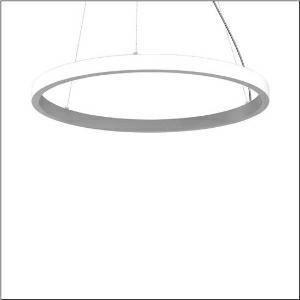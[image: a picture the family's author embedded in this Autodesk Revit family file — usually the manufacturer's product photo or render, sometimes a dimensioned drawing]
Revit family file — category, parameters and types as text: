
# Revit family: silica_r__21_ring-o_5pjbo4d1204a_97b4
name_source: partatom
category: Lighting Fixtures
units: mm (PartAtom-declared; Revit-internal decimal feet)

## family parameters
Cut with Voids When Loaded = No
Host = Face
Light Source = No
Part Type = Normal
Room Calculation Point = No
Round Connector Dimension = Use Diameter
Shared = No

## types (1)
- Silica® 21 Ring-O (1 x LED, 8820 lm, 343 W, 3000K)
    Apparent Load = 343 VA
    CIE Flux Codes = 2 16 49 50 100
    Color Rendering = 80
    Color Temperature = 3000K
    Default Elevation = 1800 mm
    Description = Silica® 21 Ring-O, suspended luminaire, of PMMA, frosted, light emission: outer ring side luminous distribution, primary light characteristic: symmetric, installation type: suspended mounting, LED, rated luminous flux: 8.820lm, luminous efficacy: 63lm/W, light colour: 830, colour temperature: 3000K, control gear: DALI 2, with terminal, 5-pole, mains connection: 230V, AC/DC, 0/50..60Hz, rated input power: 140W, housing, of extruded aluminium section, metallic grey (RAL 9006), diameter: 1.480mm, ceiling canopy, metallic grey (RAL 9006), protection rating (lamp compartment): IP40, insulation class (complete): insulation class I (protective earthing), certification: CE, impact resistance: IK02, permissible operating ambient temperature: 0..+35°C, packaging unit: 1 piece
    Height = 48 mm  [stored 0.15748 ft]
    Lamp = 1 x LED
    Lamp Light Flux = 8820 lm
    Lamp Power = 343 W
    Lamp count = 1
    Length = 1480 mm
    Luminous efficacy = 26 lm/W
    Manufacturer = Siteco
    ModVariant = No
    Model = 5PJBO4D1204A
    Mounting Place = Ceiling
    Mounting Type = Pendant
    Number of Poles = 1
    OnlyDefault = Yes
    Power Factor = 1
    Product Name = Silica® 21 Ring-O
    Product group = suspended luminaire
    ProductGroupID = 904
    Protection Class = Protection class I
    Protection Degree = IP 40
    RLX_Detail_Level = 1
    RLX_Emergency_Light_Flux = 0 lm
    RLX_Emergency_Type = 0
    RLX_Emergency_Type_DB = No
    RlxData = <blob elided: 18429 chars, md5=1beb1126>
    Socket = socket
    Standby Power = 0 W
    System Light Flux = 8819 lm
    System Power = 343 W
    Type Comments = Product without accessories
    Type Image = l_1251764.jpg
    URL = http://relux.com
    VarID = ---
    Voltage = 0 V
    Weight = 0.00 kg
    Width = 0 mm  [stored 0 ft]

note: [stored X ft] marks values corroborated as IEEE doubles in the binary element streams (Revit-internal decimal feet)

## geometry (parser evidence)
native form markers: Blend x4, Sweep x13
no freeform markers — native parametric forms only
